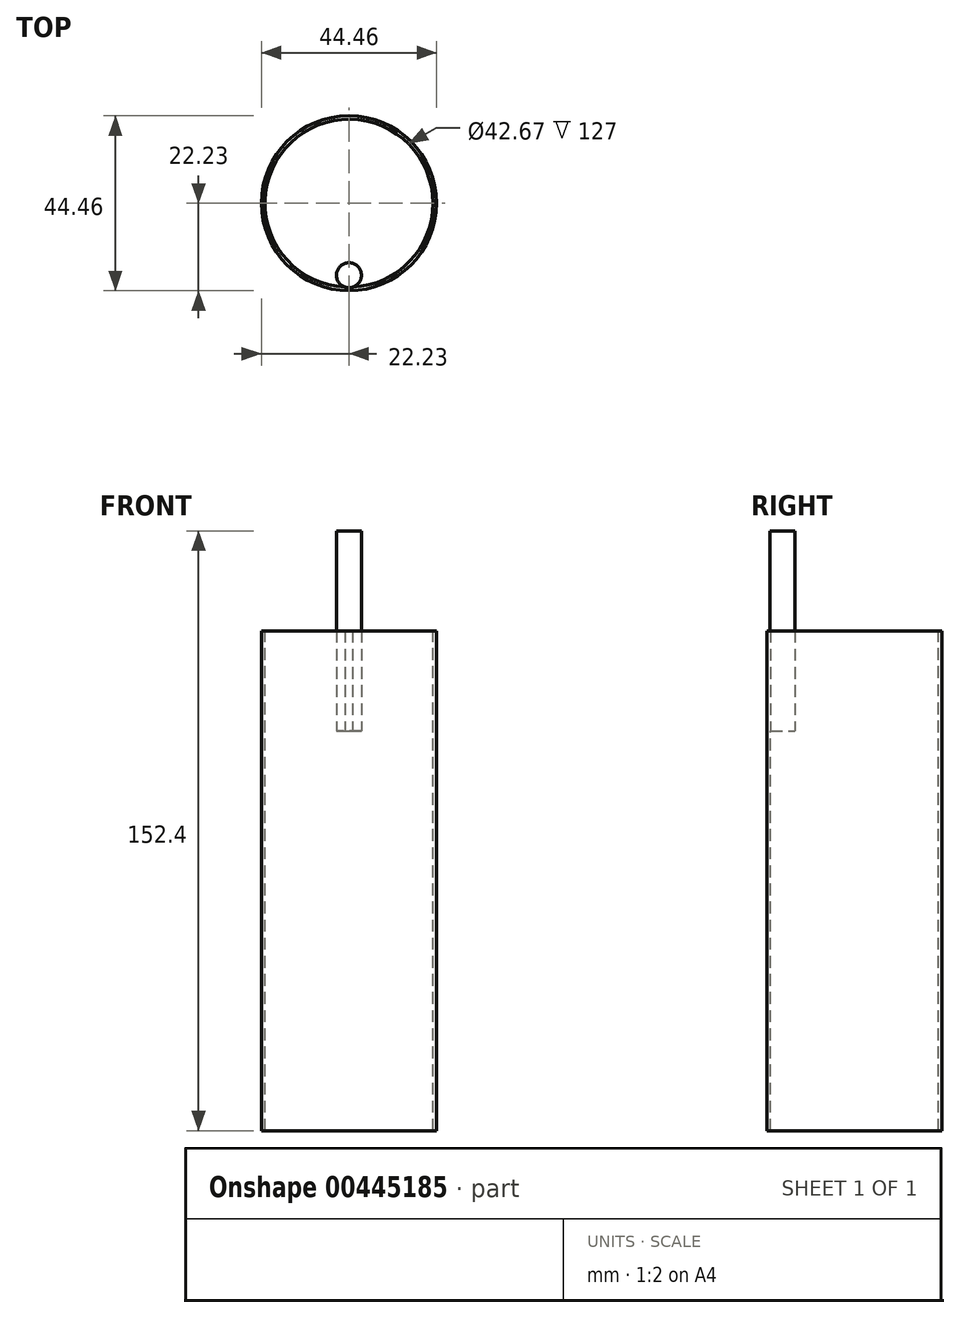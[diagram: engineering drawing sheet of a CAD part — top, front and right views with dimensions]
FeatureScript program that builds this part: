
annotation { "Feature Type Name" : "Feature", "Feature Type Description" : "" }
export const myFeature = defineFeature(function(context is Context, id is Id, definition is map)
    precondition{}
    {
        {
            var Q0;
            Q0=qCreatedBy(makeId("Top.planeOp"),FACE);
            var sketch = newSketch(context, id + "F0", { "sketchPlane" : qUnion([Q0])});
            skCircle(sketch, "E0", {"center": v(0, 0) * mm, "radius": 22.22 * mm});
            skCircle(sketch, "E1", {"center": v(0, 0) * mm, "radius": 21.34 * mm});
            skSolve(sketch);
        }
        {
            var Q0;
            Q0 = qSketchRegion(id + "F0", true);
            extrude(context, id + "F1", {"entities" : qUnion([Q0]), "oppositeDirection" : true, "depth" : 127 * mm});
        }
        {
            var Q0;
            Q0=makeQuery(id+"F1.opExtrude","CAP_FACE",FACE,{"disambiguationData":[OSD([sQuery(id+"F0.wireOp",EDGE,"E0"),sQuery(id+"F0.wireOp",EDGE,"E1")])],"isStart":true});
            var sketch = newSketch(context, id + "F2", { "sketchPlane" : qUnion([Q0])});
            skCircle(sketch, "E2", {"center": v(0, -18.29) * mm, "radius": 3.18 * mm});
            skSolve(sketch);
        }
        {
            var Q0;
            Q0 = qSketchRegion(id + "F2", true);
            extrude(context, id + "F3", {"entities" : qUnion([Q0]), "operationType" : NewBodyOperationType.ADD, "depth" : 25.4 * mm, "hasSecondDirection" : true, "secondDirectionOppositeDirection" : true, "secondDirectionDepth" : 25.4 * mm});
        }
    });
